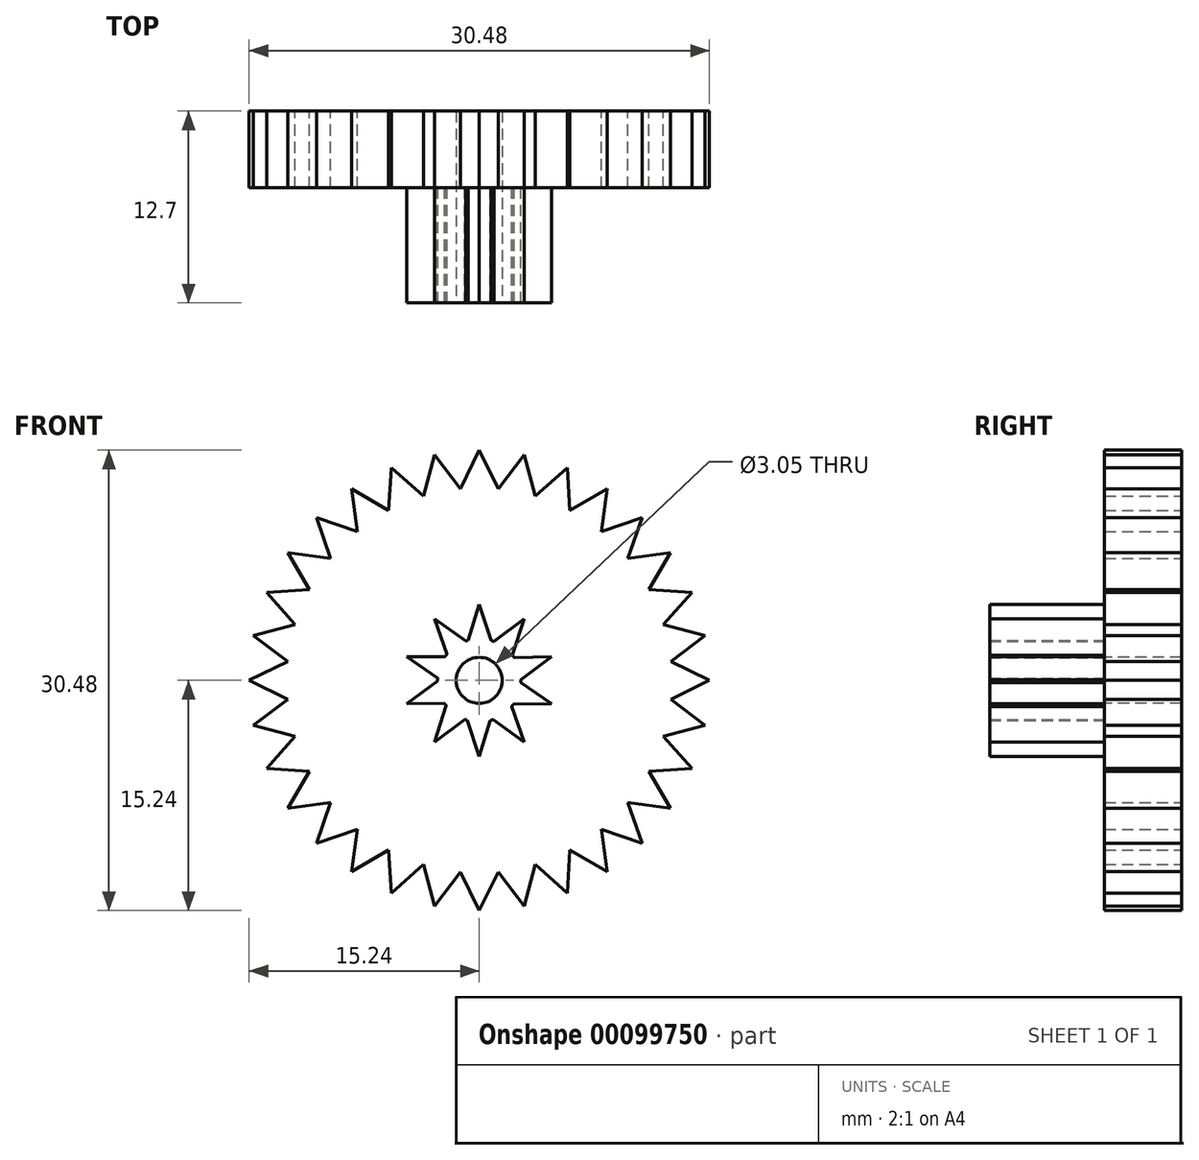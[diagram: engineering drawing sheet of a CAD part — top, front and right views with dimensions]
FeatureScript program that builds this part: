
annotation { "Feature Type Name" : "Feature", "Feature Type Description" : "" }
export const myFeature = defineFeature(function(context is Context, id is Id, definition is map)
    precondition{}
    {
        {
            var Q0;
            Q0=qCreatedBy(makeId("Front.planeOp"),FACE);
            var sketch = newSketch(context, id + "F0", { "sketchPlane" : qUnion([Q0])});
            skCircle(sketch, "E0", {"center": v(0, 0) * mm, "radius": 12.7 * mm});
            skLineSegment(sketch, "E1", {"start": v(1.27, 12.64) * mm, "end": v(0, 15.24) * mm});
            skLineSegment(sketch, "E2", {"start": v(0, 15.24) * mm, "end": v(-1.27, 12.64) * mm});
            skLineSegment(sketch, "E3.1.0", {"start": v(-2.97, 14.95) * mm, "end": v(-3.71, 12.15) * mm});
            skLineSegment(sketch, "E3.1.1", {"start": v(-1.22, 12.64) * mm, "end": v(-2.97, 14.95) * mm});
            skLineSegment(sketch, "E3.2.0", {"start": v(-5.83, 14.08) * mm, "end": v(-6, 11.19) * mm});
            skLineSegment(sketch, "E3.2.1", {"start": v(-3.66, 12.16) * mm, "end": v(-5.83, 14.08) * mm});
            skLineSegment(sketch, "E4.2.3.0", {"start": v(-8.47, 12.67) * mm, "end": v(-8.08, 9.8) * mm});
            skLineSegment(sketch, "E4.3.3.0", {"start": v(-5.96, 11.21) * mm, "end": v(-8.47, 12.67) * mm});
            skLineSegment(sketch, "E4.2.4.0", {"start": v(-10.78, 10.78) * mm, "end": v(-9.83, 8.04) * mm});
            skLineSegment(sketch, "E4.3.4.0", {"start": v(-8.04, 9.83) * mm, "end": v(-10.78, 10.78) * mm});
            skLineSegment(sketch, "E4.2.5.0", {"start": v(-12.67, 8.47) * mm, "end": v(-11.21, 5.96) * mm});
            skLineSegment(sketch, "E4.3.5.0", {"start": v(-9.8, 8.08) * mm, "end": v(-12.67, 8.47) * mm});
            skLineSegment(sketch, "E4.2.6.0", {"start": v(-14.08, 5.83) * mm, "end": v(-12.16, 3.66) * mm});
            skLineSegment(sketch, "E4.3.6.0", {"start": v(-11.19, 6) * mm, "end": v(-14.08, 5.83) * mm});
            skLineSegment(sketch, "E4.2.7.0", {"start": v(-14.95, 2.97) * mm, "end": v(-12.64, 1.22) * mm});
            skLineSegment(sketch, "E4.3.7.0", {"start": v(-12.15, 3.71) * mm, "end": v(-14.95, 2.97) * mm});
            skLineSegment(sketch, "E4.2.8.0", {"start": v(-15.24, 0) * mm, "end": v(-12.64, -1.27) * mm});
            skLineSegment(sketch, "E4.3.8.0", {"start": v(-12.64, 1.27) * mm, "end": v(-15.24, 0) * mm});
            skLineSegment(sketch, "E4.2.9.0", {"start": v(-14.95, -2.97) * mm, "end": v(-12.15, -3.71) * mm});
            skLineSegment(sketch, "E4.3.9.0", {"start": v(-12.64, -1.22) * mm, "end": v(-14.95, -2.97) * mm});
            skLineSegment(sketch, "E4.2.10.0", {"start": v(-14.08, -5.83) * mm, "end": v(-11.19, -6) * mm});
            skLineSegment(sketch, "E4.3.10.0", {"start": v(-12.16, -3.66) * mm, "end": v(-14.08, -5.83) * mm});
            skLineSegment(sketch, "E4.2.11.0", {"start": v(-12.67, -8.47) * mm, "end": v(-9.8, -8.08) * mm});
            skLineSegment(sketch, "E4.3.11.0", {"start": v(-11.21, -5.96) * mm, "end": v(-12.67, -8.47) * mm});
            skLineSegment(sketch, "E4.2.12.0", {"start": v(-10.78, -10.78) * mm, "end": v(-8.04, -9.83) * mm});
            skLineSegment(sketch, "E4.3.12.0", {"start": v(-9.83, -8.04) * mm, "end": v(-10.78, -10.78) * mm});
            skLineSegment(sketch, "E4.2.13.0", {"start": v(-8.47, -12.67) * mm, "end": v(-5.96, -11.21) * mm});
            skLineSegment(sketch, "E4.3.13.0", {"start": v(-8.08, -9.8) * mm, "end": v(-8.47, -12.67) * mm});
            skLineSegment(sketch, "E4.2.14.0", {"start": v(-5.83, -14.08) * mm, "end": v(-3.66, -12.16) * mm});
            skLineSegment(sketch, "E4.3.14.0", {"start": v(-6, -11.19) * mm, "end": v(-5.83, -14.08) * mm});
            skLineSegment(sketch, "E4.2.15.0", {"start": v(-2.97, -14.95) * mm, "end": v(-1.22, -12.64) * mm});
            skLineSegment(sketch, "E4.3.15.0", {"start": v(-3.71, -12.15) * mm, "end": v(-2.97, -14.95) * mm});
            skLineSegment(sketch, "E4.2.16.0", {"start": v(0, -15.24) * mm, "end": v(1.27, -12.64) * mm});
            skLineSegment(sketch, "E4.3.16.0", {"start": v(-1.27, -12.64) * mm, "end": v(0, -15.24) * mm});
            skLineSegment(sketch, "E4.2.17.0", {"start": v(2.97, -14.95) * mm, "end": v(3.71, -12.15) * mm});
            skLineSegment(sketch, "E4.3.17.0", {"start": v(1.22, -12.64) * mm, "end": v(2.97, -14.95) * mm});
            skLineSegment(sketch, "E4.2.18.0", {"start": v(5.83, -14.08) * mm, "end": v(6, -11.19) * mm});
            skLineSegment(sketch, "E4.3.18.0", {"start": v(3.66, -12.16) * mm, "end": v(5.83, -14.08) * mm});
            skLineSegment(sketch, "E4.2.19.0", {"start": v(8.47, -12.67) * mm, "end": v(8.08, -9.8) * mm});
            skLineSegment(sketch, "E4.3.19.0", {"start": v(5.96, -11.21) * mm, "end": v(8.47, -12.67) * mm});
            skLineSegment(sketch, "E4.2.20.0", {"start": v(10.78, -10.78) * mm, "end": v(9.83, -8.04) * mm});
            skLineSegment(sketch, "E4.3.20.0", {"start": v(8.04, -9.83) * mm, "end": v(10.78, -10.78) * mm});
            skLineSegment(sketch, "E4.2.21.0", {"start": v(12.67, -8.47) * mm, "end": v(11.21, -5.96) * mm});
            skLineSegment(sketch, "E4.3.21.0", {"start": v(9.8, -8.08) * mm, "end": v(12.67, -8.47) * mm});
            skLineSegment(sketch, "E4.2.22.0", {"start": v(14.08, -5.83) * mm, "end": v(12.16, -3.66) * mm});
            skLineSegment(sketch, "E4.3.22.0", {"start": v(11.19, -6) * mm, "end": v(14.08, -5.83) * mm});
            skLineSegment(sketch, "E4.2.23.0", {"start": v(14.95, -2.97) * mm, "end": v(12.64, -1.22) * mm});
            skLineSegment(sketch, "E4.3.23.0", {"start": v(12.15, -3.71) * mm, "end": v(14.95, -2.97) * mm});
            skLineSegment(sketch, "E4.2.24.0", {"start": v(15.24, 0) * mm, "end": v(12.64, 1.27) * mm});
            skLineSegment(sketch, "E4.3.24.0", {"start": v(12.64, -1.27) * mm, "end": v(15.24, 0) * mm});
            skLineSegment(sketch, "E4.2.25.0", {"start": v(14.95, 2.97) * mm, "end": v(12.15, 3.71) * mm});
            skLineSegment(sketch, "E4.3.25.0", {"start": v(12.64, 1.22) * mm, "end": v(14.95, 2.97) * mm});
            skLineSegment(sketch, "E4.2.26.0", {"start": v(14.08, 5.83) * mm, "end": v(11.19, 6) * mm});
            skLineSegment(sketch, "E4.3.26.0", {"start": v(12.16, 3.66) * mm, "end": v(14.08, 5.83) * mm});
            skLineSegment(sketch, "E4.2.27.0", {"start": v(12.67, 8.47) * mm, "end": v(9.8, 8.08) * mm});
            skLineSegment(sketch, "E4.3.27.0", {"start": v(11.21, 5.96) * mm, "end": v(12.67, 8.47) * mm});
            skLineSegment(sketch, "E4.2.28.0", {"start": v(10.78, 10.78) * mm, "end": v(8.04, 9.83) * mm});
            skLineSegment(sketch, "E4.3.28.0", {"start": v(9.83, 8.04) * mm, "end": v(10.78, 10.78) * mm});
            skLineSegment(sketch, "E4.2.29.0", {"start": v(8.47, 12.67) * mm, "end": v(5.96, 11.21) * mm});
            skLineSegment(sketch, "E4.3.29.0", {"start": v(8.08, 9.8) * mm, "end": v(8.47, 12.67) * mm});
            skLineSegment(sketch, "E4.2.30.0", {"start": v(5.83, 14.08) * mm, "end": v(3.66, 12.16) * mm});
            skLineSegment(sketch, "E4.3.30.0", {"start": v(6, 11.19) * mm, "end": v(5.83, 14.08) * mm});
            skLineSegment(sketch, "E4.2.31.0", {"start": v(2.97, 14.95) * mm, "end": v(1.22, 12.64) * mm});
            skLineSegment(sketch, "E4.3.31.0", {"start": v(3.71, 12.15) * mm, "end": v(2.97, 14.95) * mm});
            skSolve(sketch);
        }
        {
            var Q0;
            {var subQ3=sQuery(id+"F0.wireOp",EDGE,"E3.1.0");var subQ5=sQuery(id+"F0.wireOp",EDGE,"E0");var subQ6=makeQuery(id+"F0.imprint","INTERSECT",VERTEX,{"derivedFrom":[subQ5,subQ3]});Q0=makeQuery(id+"F0.imprint","IMPRINT",FACE,{"disambiguationData":[TD([[makeQuery(id+"F0.imprint","IMPRINT",EDGE,{"disambiguationData":[TD([[subQ6,-1.0]])],"derivedFrom":subQ5}),-1.0]])]});}
            var Q1;
            {var subQ3=sQuery(id+"F0.wireOp",EDGE,"E4.2.17.0");var subQ7=sQuery(id+"F0.wireOp",EDGE,"E0");var subQ8=makeQuery(id+"F0.imprint","INTERSECT",VERTEX,{"derivedFrom":[subQ7,subQ3]});Q1=makeQuery(id+"F0.imprint","IMPRINT",FACE,{"disambiguationData":[TD([[makeQuery(id+"F0.imprint","IMPRINT",EDGE,{"disambiguationData":[TD([[subQ8,-1.0]])],"derivedFrom":subQ7}),-1.0]])]});}
            var Q2;
            {var subQ3=sQuery(id+"F0.wireOp",EDGE,"E4.2.9.0");var subQ7=sQuery(id+"F0.wireOp",EDGE,"E0");var subQ8=makeQuery(id+"F0.imprint","INTERSECT",VERTEX,{"derivedFrom":[subQ7,subQ3]});Q2=makeQuery(id+"F0.imprint","IMPRINT",FACE,{"disambiguationData":[TD([[makeQuery(id+"F0.imprint","IMPRINT",EDGE,{"disambiguationData":[TD([[subQ8,-1.0]])],"derivedFrom":subQ7}),-1.0]])]});}
            var Q3;
            {var subQ5=sQuery(id+"F0.wireOp",EDGE,"E4.2.22.0");var subQ7=sQuery(id+"F0.wireOp",EDGE,"E0");var subQ8=makeQuery(id+"F0.imprint","INTERSECT",VERTEX,{"derivedFrom":[subQ7,subQ5]});Q3=makeQuery(id+"F0.imprint","IMPRINT",FACE,{"disambiguationData":[TD([[makeQuery(id+"F0.imprint","IMPRINT",EDGE,{"disambiguationData":[TD([[subQ8,-1.0]])],"derivedFrom":subQ7}),-1.0]])]});}
            var Q4;
            {var subQ3=sQuery(id+"F0.wireOp",EDGE,"E4.2.14.0");var subQ7=sQuery(id+"F0.wireOp",EDGE,"E0");var subQ8=makeQuery(id+"F0.imprint","INTERSECT",VERTEX,{"derivedFrom":[subQ7,subQ3]});Q4=makeQuery(id+"F0.imprint","IMPRINT",FACE,{"disambiguationData":[TD([[makeQuery(id+"F0.imprint","IMPRINT",EDGE,{"disambiguationData":[TD([[subQ8,-1.0]])],"derivedFrom":subQ7}),-1.0]])]});}
            var Q5;
            {var subQ3=sQuery(id+"F0.wireOp",EDGE,"E4.2.6.0");var subQ7=sQuery(id+"F0.wireOp",EDGE,"E0");var subQ8=makeQuery(id+"F0.imprint","INTERSECT",VERTEX,{"derivedFrom":[subQ7,subQ3]});Q5=makeQuery(id+"F0.imprint","IMPRINT",FACE,{"disambiguationData":[TD([[makeQuery(id+"F0.imprint","IMPRINT",EDGE,{"disambiguationData":[TD([[subQ8,-1.0]])],"derivedFrom":subQ7}),-1.0]])]});}
            var Q6;
            {var subQ0=sQuery(id+"F0.wireOp",EDGE,"E3.1.1");var subQ1=sQuery(id+"F0.wireOp",EDGE,"E0");var subQ2=makeQuery(id+"F0.imprint","INTERSECT",VERTEX,{"derivedFrom":[subQ1,subQ0]});Q6=makeQuery(id+"F0.imprint","IMPRINT",FACE,{"disambiguationData":[TD([[makeQuery(id+"F0.imprint","IMPRINT",EDGE,{"disambiguationData":[TD([[subQ2,1.0]])],"derivedFrom":subQ1}),-1.0]])]});}
            var Q7;
            {var subQ3=sQuery(id+"F0.wireOp",EDGE,"E1");var subQ6=sQuery(id+"F0.wireOp",EDGE,"E0");var subQ9=makeQuery(id+"F0.imprint","INTERSECT",VERTEX,{"derivedFrom":[subQ6,subQ3]});Q7=makeQuery(id+"F0.imprint","IMPRINT",FACE,{"disambiguationData":[TD([[makeQuery(id+"F0.imprint","IMPRINT",EDGE,{"disambiguationData":[TD([[subQ9,1.0]])],"derivedFrom":subQ6}),-1.0]])]});}
            var Q8;
            {var subQ0=sQuery(id+"F0.wireOp",EDGE,"E0");var subQ35=makeQuery(id+"F0.imprint","INTERSECT",VERTEX,{"derivedFrom":[subQ0,sQuery(id+"F0.wireOp",EDGE,"E4.2.24.0")]});Q8=makeQuery(id+"F0.imprint","IMPRINT",FACE,{"disambiguationData":[TD([[makeQuery(id+"F0.imprint","IMPRINT",EDGE,{"disambiguationData":[TD([[subQ35,1.0]])],"derivedFrom":subQ0}),1.0]])]});}
            var Q9;
            {var subQ3=sQuery(id+"F0.wireOp",EDGE,"E4.2.24.0");var subQ7=sQuery(id+"F0.wireOp",EDGE,"E0");var subQ8=makeQuery(id+"F0.imprint","INTERSECT",VERTEX,{"derivedFrom":[subQ7,subQ3]});Q9=makeQuery(id+"F0.imprint","IMPRINT",FACE,{"disambiguationData":[TD([[makeQuery(id+"F0.imprint","IMPRINT",EDGE,{"disambiguationData":[TD([[subQ8,-1.0]])],"derivedFrom":subQ7}),-1.0]])]});}
            var Q10;
            {var subQ3=sQuery(id+"F0.wireOp",EDGE,"E4.2.25.0");var subQ5=sQuery(id+"F0.wireOp",EDGE,"E0");var subQ6=makeQuery(id+"F0.imprint","INTERSECT",VERTEX,{"derivedFrom":[subQ5,subQ3]});Q10=makeQuery(id+"F0.imprint","IMPRINT",FACE,{"disambiguationData":[TD([[makeQuery(id+"F0.imprint","IMPRINT",EDGE,{"disambiguationData":[TD([[subQ6,-1.0]])],"derivedFrom":subQ5}),-1.0]])]});}
            var Q11;
            {var subQ5=sQuery(id+"F0.wireOp",EDGE,"E4.2.26.0");var subQ7=sQuery(id+"F0.wireOp",EDGE,"E0");var subQ8=makeQuery(id+"F0.imprint","INTERSECT",VERTEX,{"derivedFrom":[subQ7,subQ5]});Q11=makeQuery(id+"F0.imprint","IMPRINT",FACE,{"disambiguationData":[TD([[makeQuery(id+"F0.imprint","IMPRINT",EDGE,{"disambiguationData":[TD([[subQ8,-1.0]])],"derivedFrom":subQ7}),-1.0]])]});}
            var Q12;
            {var subQ5=sQuery(id+"F0.wireOp",EDGE,"E4.2.27.0");var subQ6=sQuery(id+"F0.wireOp",EDGE,"E0");var subQ7=makeQuery(id+"F0.imprint","INTERSECT",VERTEX,{"derivedFrom":[subQ6,subQ5]});Q12=makeQuery(id+"F0.imprint","IMPRINT",FACE,{"disambiguationData":[TD([[makeQuery(id+"F0.imprint","IMPRINT",EDGE,{"disambiguationData":[TD([[subQ7,-1.0]])],"derivedFrom":subQ6}),-1.0]])]});}
            var Q13;
            {var subQ3=sQuery(id+"F0.wireOp",EDGE,"E4.2.28.0");var subQ7=sQuery(id+"F0.wireOp",EDGE,"E0");var subQ8=makeQuery(id+"F0.imprint","INTERSECT",VERTEX,{"derivedFrom":[subQ7,subQ3]});Q13=makeQuery(id+"F0.imprint","IMPRINT",FACE,{"disambiguationData":[TD([[makeQuery(id+"F0.imprint","IMPRINT",EDGE,{"disambiguationData":[TD([[subQ8,-1.0]])],"derivedFrom":subQ7}),-1.0]])]});}
            var Q14;
            {var subQ5=sQuery(id+"F0.wireOp",EDGE,"E4.2.29.0");var subQ6=sQuery(id+"F0.wireOp",EDGE,"E0");var subQ7=makeQuery(id+"F0.imprint","INTERSECT",VERTEX,{"derivedFrom":[subQ6,subQ5]});Q14=makeQuery(id+"F0.imprint","IMPRINT",FACE,{"disambiguationData":[TD([[makeQuery(id+"F0.imprint","IMPRINT",EDGE,{"disambiguationData":[TD([[subQ7,-1.0]])],"derivedFrom":subQ6}),-1.0]])]});}
            var Q15;
            {var subQ3=sQuery(id+"F0.wireOp",EDGE,"E4.2.21.0");var subQ7=sQuery(id+"F0.wireOp",EDGE,"E0");var subQ8=makeQuery(id+"F0.imprint","INTERSECT",VERTEX,{"derivedFrom":[subQ7,subQ3]});Q15=makeQuery(id+"F0.imprint","IMPRINT",FACE,{"disambiguationData":[TD([[makeQuery(id+"F0.imprint","IMPRINT",EDGE,{"disambiguationData":[TD([[subQ8,-1.0]])],"derivedFrom":subQ7}),-1.0]])]});}
            var Q16;
            {var subQ3=sQuery(id+"F0.wireOp",EDGE,"E4.2.13.0");var subQ5=sQuery(id+"F0.wireOp",EDGE,"E0");var subQ6=makeQuery(id+"F0.imprint","INTERSECT",VERTEX,{"derivedFrom":[subQ5,subQ3]});Q16=makeQuery(id+"F0.imprint","IMPRINT",FACE,{"disambiguationData":[TD([[makeQuery(id+"F0.imprint","IMPRINT",EDGE,{"disambiguationData":[TD([[subQ6,-1.0]])],"derivedFrom":subQ5}),-1.0]])]});}
            var Q17;
            {var subQ3=sQuery(id+"F0.wireOp",EDGE,"E4.2.5.0");var subQ5=sQuery(id+"F0.wireOp",EDGE,"E0");var subQ6=makeQuery(id+"F0.imprint","INTERSECT",VERTEX,{"derivedFrom":[subQ5,subQ3]});Q17=makeQuery(id+"F0.imprint","IMPRINT",FACE,{"disambiguationData":[TD([[makeQuery(id+"F0.imprint","IMPRINT",EDGE,{"disambiguationData":[TD([[subQ6,-1.0]])],"derivedFrom":subQ5}),-1.0]])]});}
            var Q18;
            {var subQ3=sQuery(id+"F0.wireOp",EDGE,"E4.2.19.0");var subQ5=sQuery(id+"F0.wireOp",EDGE,"E0");var subQ6=makeQuery(id+"F0.imprint","INTERSECT",VERTEX,{"derivedFrom":[subQ5,subQ3]});Q18=makeQuery(id+"F0.imprint","IMPRINT",FACE,{"disambiguationData":[TD([[makeQuery(id+"F0.imprint","IMPRINT",EDGE,{"disambiguationData":[TD([[subQ6,-1.0]])],"derivedFrom":subQ5}),-1.0]])]});}
            var Q19;
            {var subQ5=sQuery(id+"F0.wireOp",EDGE,"E4.2.11.0");var subQ6=sQuery(id+"F0.wireOp",EDGE,"E0");var subQ7=makeQuery(id+"F0.imprint","INTERSECT",VERTEX,{"derivedFrom":[subQ6,subQ5]});Q19=makeQuery(id+"F0.imprint","IMPRINT",FACE,{"disambiguationData":[TD([[makeQuery(id+"F0.imprint","IMPRINT",EDGE,{"disambiguationData":[TD([[subQ7,-1.0]])],"derivedFrom":subQ6}),-1.0]])]});}
            var Q20;
            {var subQ5=sQuery(id+"F0.wireOp",EDGE,"E4.2.3.0");var subQ6=sQuery(id+"F0.wireOp",EDGE,"E0");var subQ7=makeQuery(id+"F0.imprint","INTERSECT",VERTEX,{"derivedFrom":[subQ6,subQ5]});Q20=makeQuery(id+"F0.imprint","IMPRINT",FACE,{"disambiguationData":[TD([[makeQuery(id+"F0.imprint","IMPRINT",EDGE,{"disambiguationData":[TD([[subQ7,-1.0]])],"derivedFrom":subQ6}),-1.0]])]});}
            var Q21;
            {var subQ3=sQuery(id+"F0.wireOp",EDGE,"E3.2.0");var subQ7=sQuery(id+"F0.wireOp",EDGE,"E0");var subQ9=makeQuery(id+"F0.imprint","INTERSECT",VERTEX,{"derivedFrom":[subQ7,subQ3]});Q21=makeQuery(id+"F0.imprint","IMPRINT",FACE,{"disambiguationData":[TD([[makeQuery(id+"F0.imprint","IMPRINT",EDGE,{"disambiguationData":[TD([[subQ9,-1.0]])],"derivedFrom":subQ7}),-1.0]])]});}
            var Q22;
            {var subQ3=sQuery(id+"F0.wireOp",EDGE,"E4.2.18.0");var subQ7=sQuery(id+"F0.wireOp",EDGE,"E0");var subQ8=makeQuery(id+"F0.imprint","INTERSECT",VERTEX,{"derivedFrom":[subQ7,subQ3]});Q22=makeQuery(id+"F0.imprint","IMPRINT",FACE,{"disambiguationData":[TD([[makeQuery(id+"F0.imprint","IMPRINT",EDGE,{"disambiguationData":[TD([[subQ8,-1.0]])],"derivedFrom":subQ7}),-1.0]])]});}
            var Q23;
            {var subQ3=sQuery(id+"F0.wireOp",EDGE,"E4.2.10.0");var subQ7=sQuery(id+"F0.wireOp",EDGE,"E0");var subQ8=makeQuery(id+"F0.imprint","INTERSECT",VERTEX,{"derivedFrom":[subQ7,subQ3]});Q23=makeQuery(id+"F0.imprint","IMPRINT",FACE,{"disambiguationData":[TD([[makeQuery(id+"F0.imprint","IMPRINT",EDGE,{"disambiguationData":[TD([[subQ8,-1.0]])],"derivedFrom":subQ7}),-1.0]])]});}
            var Q24;
            {var subQ0=sQuery(id+"F0.wireOp",EDGE,"E2");var subQ1=sQuery(id+"F0.wireOp",EDGE,"E0");var subQ2=makeQuery(id+"F0.imprint","INTERSECT",VERTEX,{"derivedFrom":[subQ1,subQ0]});Q24=makeQuery(id+"F0.imprint","IMPRINT",FACE,{"disambiguationData":[TD([[makeQuery(id+"F0.imprint","IMPRINT",EDGE,{"disambiguationData":[TD([[subQ2,-1.0]])],"derivedFrom":subQ1}),-1.0]])]});}
            var Q25;
            {var subQ0=sQuery(id+"F0.wireOp",EDGE,"E4.2.16.0");var subQ1=sQuery(id+"F0.wireOp",EDGE,"E0");var subQ2=makeQuery(id+"F0.imprint","INTERSECT",VERTEX,{"derivedFrom":[subQ1,subQ0]});Q25=makeQuery(id+"F0.imprint","IMPRINT",FACE,{"disambiguationData":[TD([[makeQuery(id+"F0.imprint","IMPRINT",EDGE,{"disambiguationData":[TD([[subQ2,-1.0]])],"derivedFrom":subQ1}),-1.0]])]});}
            var Q26;
            {var subQ3=sQuery(id+"F0.wireOp",EDGE,"E4.2.8.0");var subQ5=sQuery(id+"F0.wireOp",EDGE,"E0");var subQ6=makeQuery(id+"F0.imprint","INTERSECT",VERTEX,{"derivedFrom":[subQ5,subQ3]});Q26=makeQuery(id+"F0.imprint","IMPRINT",FACE,{"disambiguationData":[TD([[makeQuery(id+"F0.imprint","IMPRINT",EDGE,{"disambiguationData":[TD([[subQ6,-1.0]])],"derivedFrom":subQ5}),-1.0]])]});}
            var Q27;
            {var subQ3=sQuery(id+"F0.wireOp",EDGE,"E4.2.7.0");var subQ7=sQuery(id+"F0.wireOp",EDGE,"E0");var subQ8=makeQuery(id+"F0.imprint","INTERSECT",VERTEX,{"derivedFrom":[subQ7,subQ3]});Q27=makeQuery(id+"F0.imprint","IMPRINT",FACE,{"disambiguationData":[TD([[makeQuery(id+"F0.imprint","IMPRINT",EDGE,{"disambiguationData":[TD([[subQ8,-1.0]])],"derivedFrom":subQ7}),-1.0]])]});}
            var Q28;
            {var subQ5=sQuery(id+"F0.wireOp",EDGE,"E4.2.20.0");var subQ6=sQuery(id+"F0.wireOp",EDGE,"E0");var subQ7=makeQuery(id+"F0.imprint","INTERSECT",VERTEX,{"derivedFrom":[subQ6,subQ5]});Q28=makeQuery(id+"F0.imprint","IMPRINT",FACE,{"disambiguationData":[TD([[makeQuery(id+"F0.imprint","IMPRINT",EDGE,{"disambiguationData":[TD([[subQ7,-1.0]])],"derivedFrom":subQ6}),-1.0]])]});}
            var Q29;
            {var subQ3=sQuery(id+"F0.wireOp",EDGE,"E4.2.12.0");var subQ7=sQuery(id+"F0.wireOp",EDGE,"E0");var subQ8=makeQuery(id+"F0.imprint","INTERSECT",VERTEX,{"derivedFrom":[subQ7,subQ3]});Q29=makeQuery(id+"F0.imprint","IMPRINT",FACE,{"disambiguationData":[TD([[makeQuery(id+"F0.imprint","IMPRINT",EDGE,{"disambiguationData":[TD([[subQ8,-1.0]])],"derivedFrom":subQ7}),-1.0]])]});}
            var Q30;
            {var subQ5=sQuery(id+"F0.wireOp",EDGE,"E0");var subQ7=sQuery(id+"F0.wireOp",EDGE,"E4.2.4.0");var subQ9=makeQuery(id+"F0.imprint","INTERSECT",VERTEX,{"derivedFrom":[subQ5,subQ7]});Q30=makeQuery(id+"F0.imprint","IMPRINT",FACE,{"disambiguationData":[TD([[makeQuery(id+"F0.imprint","IMPRINT",EDGE,{"disambiguationData":[TD([[subQ9,-1.0]])],"derivedFrom":subQ5}),-1.0]])]});}
            var Q31;
            {var subQ3=sQuery(id+"F0.wireOp",EDGE,"E4.2.15.0");var subQ7=sQuery(id+"F0.wireOp",EDGE,"E0");var subQ8=makeQuery(id+"F0.imprint","INTERSECT",VERTEX,{"derivedFrom":[subQ7,subQ3]});Q31=makeQuery(id+"F0.imprint","IMPRINT",FACE,{"disambiguationData":[TD([[makeQuery(id+"F0.imprint","IMPRINT",EDGE,{"disambiguationData":[TD([[subQ8,-1.0]])],"derivedFrom":subQ7}),-1.0]])]});}
            var Q32;
            {var subQ0=sQuery(id+"F0.wireOp",EDGE,"E4.2.19.0");var subQ1=sQuery(id+"F0.wireOp",EDGE,"E0");var subQ2=makeQuery(id+"F0.imprint","INTERSECT",VERTEX,{"derivedFrom":[subQ1,subQ0]});Q32=makeQuery(id+"F0.imprint","IMPRINT",FACE,{"disambiguationData":[TD([[makeQuery(id+"F0.imprint","IMPRINT",EDGE,{"disambiguationData":[TD([[subQ2,1.0]])],"derivedFrom":subQ1}),-1.0]])]});}
            var Q33;
            {var subQ0=sQuery(id+"F0.wireOp",EDGE,"E4.2.28.0");var subQ1=sQuery(id+"F0.wireOp",EDGE,"E0");var subQ2=makeQuery(id+"F0.imprint","INTERSECT",VERTEX,{"derivedFrom":[subQ1,subQ0]});Q33=makeQuery(id+"F0.imprint","IMPRINT",FACE,{"disambiguationData":[TD([[makeQuery(id+"F0.imprint","IMPRINT",EDGE,{"disambiguationData":[TD([[subQ2,1.0]])],"derivedFrom":subQ1}),-1.0]])]});}
            var Q34;
            {var subQ3=sQuery(id+"F0.wireOp",EDGE,"E4.2.23.0");var subQ7=sQuery(id+"F0.wireOp",EDGE,"E0");var subQ8=makeQuery(id+"F0.imprint","INTERSECT",VERTEX,{"derivedFrom":[subQ7,subQ3]});Q34=makeQuery(id+"F0.imprint","IMPRINT",FACE,{"disambiguationData":[TD([[makeQuery(id+"F0.imprint","IMPRINT",EDGE,{"disambiguationData":[TD([[subQ8,-1.0]])],"derivedFrom":subQ7}),-1.0]])]});}
            var Q35;
            {var subQ0=sQuery(id+"F0.wireOp",EDGE,"E4.2.21.0");var subQ1=sQuery(id+"F0.wireOp",EDGE,"E0");var subQ2=makeQuery(id+"F0.imprint","INTERSECT",VERTEX,{"derivedFrom":[subQ1,subQ0]});Q35=makeQuery(id+"F0.imprint","IMPRINT",FACE,{"disambiguationData":[TD([[makeQuery(id+"F0.imprint","IMPRINT",EDGE,{"disambiguationData":[TD([[subQ2,1.0]])],"derivedFrom":subQ1}),-1.0]])]});}
            var Q36;
            {var subQ0=sQuery(id+"F0.wireOp",EDGE,"E4.2.13.0");var subQ1=sQuery(id+"F0.wireOp",EDGE,"E0");var subQ2=makeQuery(id+"F0.imprint","INTERSECT",VERTEX,{"derivedFrom":[subQ1,subQ0]});Q36=makeQuery(id+"F0.imprint","IMPRINT",FACE,{"disambiguationData":[TD([[makeQuery(id+"F0.imprint","IMPRINT",EDGE,{"disambiguationData":[TD([[subQ2,1.0]])],"derivedFrom":subQ1}),-1.0]])]});}
            var Q37;
            {var subQ0=sQuery(id+"F0.wireOp",EDGE,"E4.2.5.0");var subQ1=sQuery(id+"F0.wireOp",EDGE,"E0");var subQ2=makeQuery(id+"F0.imprint","INTERSECT",VERTEX,{"derivedFrom":[subQ1,subQ0]});Q37=makeQuery(id+"F0.imprint","IMPRINT",FACE,{"disambiguationData":[TD([[makeQuery(id+"F0.imprint","IMPRINT",EDGE,{"disambiguationData":[TD([[subQ2,1.0]])],"derivedFrom":subQ1}),-1.0]])]});}
            var Q38;
            {var subQ0=sQuery(id+"F0.wireOp",EDGE,"E4.2.11.0");var subQ1=sQuery(id+"F0.wireOp",EDGE,"E0");var subQ2=makeQuery(id+"F0.imprint","INTERSECT",VERTEX,{"derivedFrom":[subQ1,subQ0]});Q38=makeQuery(id+"F0.imprint","IMPRINT",FACE,{"disambiguationData":[TD([[makeQuery(id+"F0.imprint","IMPRINT",EDGE,{"disambiguationData":[TD([[subQ2,1.0]])],"derivedFrom":subQ1}),-1.0]])]});}
            var Q39;
            {var subQ0=sQuery(id+"F0.wireOp",EDGE,"E4.2.3.0");var subQ1=sQuery(id+"F0.wireOp",EDGE,"E0");var subQ2=makeQuery(id+"F0.imprint","INTERSECT",VERTEX,{"derivedFrom":[subQ1,subQ0]});Q39=makeQuery(id+"F0.imprint","IMPRINT",FACE,{"disambiguationData":[TD([[makeQuery(id+"F0.imprint","IMPRINT",EDGE,{"disambiguationData":[TD([[subQ2,1.0]])],"derivedFrom":subQ1}),-1.0]])]});}
            var Q40;
            {var subQ0=sQuery(id+"F0.wireOp",EDGE,"E3.2.0");var subQ1=sQuery(id+"F0.wireOp",EDGE,"E0");var subQ2=makeQuery(id+"F0.imprint","INTERSECT",VERTEX,{"derivedFrom":[subQ1,subQ0]});Q40=makeQuery(id+"F0.imprint","IMPRINT",FACE,{"disambiguationData":[TD([[makeQuery(id+"F0.imprint","IMPRINT",EDGE,{"disambiguationData":[TD([[subQ2,1.0]])],"derivedFrom":subQ1}),-1.0]])]});}
            var Q41;
            {var subQ0=sQuery(id+"F0.wireOp",EDGE,"E4.2.18.0");var subQ1=sQuery(id+"F0.wireOp",EDGE,"E0");var subQ2=makeQuery(id+"F0.imprint","INTERSECT",VERTEX,{"derivedFrom":[subQ1,subQ0]});Q41=makeQuery(id+"F0.imprint","IMPRINT",FACE,{"disambiguationData":[TD([[makeQuery(id+"F0.imprint","IMPRINT",EDGE,{"disambiguationData":[TD([[subQ2,1.0]])],"derivedFrom":subQ1}),-1.0]])]});}
            var Q42;
            {var subQ0=sQuery(id+"F0.wireOp",EDGE,"E4.2.10.0");var subQ1=sQuery(id+"F0.wireOp",EDGE,"E0");var subQ2=makeQuery(id+"F0.imprint","INTERSECT",VERTEX,{"derivedFrom":[subQ1,subQ0]});Q42=makeQuery(id+"F0.imprint","IMPRINT",FACE,{"disambiguationData":[TD([[makeQuery(id+"F0.imprint","IMPRINT",EDGE,{"disambiguationData":[TD([[subQ2,1.0]])],"derivedFrom":subQ1}),-1.0]])]});}
            var Q43;
            {var subQ0=sQuery(id+"F0.wireOp",EDGE,"E2");var subQ1=sQuery(id+"F0.wireOp",EDGE,"E0");var subQ2=makeQuery(id+"F0.imprint","INTERSECT",VERTEX,{"derivedFrom":[subQ1,subQ0]});Q43=makeQuery(id+"F0.imprint","IMPRINT",FACE,{"disambiguationData":[TD([[makeQuery(id+"F0.imprint","IMPRINT",EDGE,{"disambiguationData":[TD([[subQ2,1.0]])],"derivedFrom":subQ1}),-1.0]])]});}
            var Q44;
            {var subQ0=sQuery(id+"F0.wireOp",EDGE,"E4.2.24.0");var subQ1=sQuery(id+"F0.wireOp",EDGE,"E0");var subQ2=makeQuery(id+"F0.imprint","INTERSECT",VERTEX,{"derivedFrom":[subQ1,subQ0]});Q44=makeQuery(id+"F0.imprint","IMPRINT",FACE,{"disambiguationData":[TD([[makeQuery(id+"F0.imprint","IMPRINT",EDGE,{"disambiguationData":[TD([[subQ2,1.0]])],"derivedFrom":subQ1}),-1.0]])]});}
            var Q45;
            {var subQ0=sQuery(id+"F0.wireOp",EDGE,"E4.2.23.0");var subQ1=sQuery(id+"F0.wireOp",EDGE,"E0");var subQ2=makeQuery(id+"F0.imprint","INTERSECT",VERTEX,{"derivedFrom":[subQ1,subQ0]});Q45=makeQuery(id+"F0.imprint","IMPRINT",FACE,{"disambiguationData":[TD([[makeQuery(id+"F0.imprint","IMPRINT",EDGE,{"disambiguationData":[TD([[subQ2,1.0]])],"derivedFrom":subQ1}),-1.0]])]});}
            var Q46;
            {var subQ0=sQuery(id+"F0.wireOp",EDGE,"E4.2.7.0");var subQ1=sQuery(id+"F0.wireOp",EDGE,"E0");var subQ2=makeQuery(id+"F0.imprint","INTERSECT",VERTEX,{"derivedFrom":[subQ1,subQ0]});Q46=makeQuery(id+"F0.imprint","IMPRINT",FACE,{"disambiguationData":[TD([[makeQuery(id+"F0.imprint","IMPRINT",EDGE,{"disambiguationData":[TD([[subQ2,1.0]])],"derivedFrom":subQ1}),-1.0]])]});}
            var Q47;
            {var subQ0=sQuery(id+"F0.wireOp",EDGE,"E4.2.22.0");var subQ1=sQuery(id+"F0.wireOp",EDGE,"E0");var subQ2=makeQuery(id+"F0.imprint","INTERSECT",VERTEX,{"derivedFrom":[subQ1,subQ0]});Q47=makeQuery(id+"F0.imprint","IMPRINT",FACE,{"disambiguationData":[TD([[makeQuery(id+"F0.imprint","IMPRINT",EDGE,{"disambiguationData":[TD([[subQ2,1.0]])],"derivedFrom":subQ1}),-1.0]])]});}
            var Q48;
            {var subQ0=sQuery(id+"F0.wireOp",EDGE,"E4.2.6.0");var subQ1=sQuery(id+"F0.wireOp",EDGE,"E0");var subQ2=makeQuery(id+"F0.imprint","INTERSECT",VERTEX,{"derivedFrom":[subQ1,subQ0]});Q48=makeQuery(id+"F0.imprint","IMPRINT",FACE,{"disambiguationData":[TD([[makeQuery(id+"F0.imprint","IMPRINT",EDGE,{"disambiguationData":[TD([[subQ2,1.0]])],"derivedFrom":subQ1}),-1.0]])]});}
            var Q49;
            {var subQ0=sQuery(id+"F0.wireOp",EDGE,"E4.2.20.0");var subQ1=sQuery(id+"F0.wireOp",EDGE,"E0");var subQ2=makeQuery(id+"F0.imprint","INTERSECT",VERTEX,{"derivedFrom":[subQ1,subQ0]});Q49=makeQuery(id+"F0.imprint","IMPRINT",FACE,{"disambiguationData":[TD([[makeQuery(id+"F0.imprint","IMPRINT",EDGE,{"disambiguationData":[TD([[subQ2,1.0]])],"derivedFrom":subQ1}),-1.0]])]});}
            var Q50;
            {var subQ0=sQuery(id+"F0.wireOp",EDGE,"E4.2.12.0");var subQ1=sQuery(id+"F0.wireOp",EDGE,"E0");var subQ2=makeQuery(id+"F0.imprint","INTERSECT",VERTEX,{"derivedFrom":[subQ1,subQ0]});Q50=makeQuery(id+"F0.imprint","IMPRINT",FACE,{"disambiguationData":[TD([[makeQuery(id+"F0.imprint","IMPRINT",EDGE,{"disambiguationData":[TD([[subQ2,1.0]])],"derivedFrom":subQ1}),-1.0]])]});}
            var Q51;
            {var subQ0=sQuery(id+"F0.wireOp",EDGE,"E4.2.4.0");var subQ1=sQuery(id+"F0.wireOp",EDGE,"E0");var subQ2=makeQuery(id+"F0.imprint","INTERSECT",VERTEX,{"derivedFrom":[subQ1,subQ0]});Q51=makeQuery(id+"F0.imprint","IMPRINT",FACE,{"disambiguationData":[TD([[makeQuery(id+"F0.imprint","IMPRINT",EDGE,{"disambiguationData":[TD([[subQ2,1.0]])],"derivedFrom":subQ1}),-1.0]])]});}
            var Q52;
            {var subQ0=sQuery(id+"F0.wireOp",EDGE,"E3.1.0");var subQ1=sQuery(id+"F0.wireOp",EDGE,"E0");var subQ2=makeQuery(id+"F0.imprint","INTERSECT",VERTEX,{"derivedFrom":[subQ1,subQ0]});Q52=makeQuery(id+"F0.imprint","IMPRINT",FACE,{"disambiguationData":[TD([[makeQuery(id+"F0.imprint","IMPRINT",EDGE,{"disambiguationData":[TD([[subQ2,1.0]])],"derivedFrom":subQ1}),-1.0]])]});}
            var Q53;
            {var subQ0=sQuery(id+"F0.wireOp",EDGE,"E4.2.17.0");var subQ1=sQuery(id+"F0.wireOp",EDGE,"E0");var subQ2=makeQuery(id+"F0.imprint","INTERSECT",VERTEX,{"derivedFrom":[subQ1,subQ0]});Q53=makeQuery(id+"F0.imprint","IMPRINT",FACE,{"disambiguationData":[TD([[makeQuery(id+"F0.imprint","IMPRINT",EDGE,{"disambiguationData":[TD([[subQ2,1.0]])],"derivedFrom":subQ1}),-1.0]])]});}
            var Q54;
            {var subQ0=sQuery(id+"F0.wireOp",EDGE,"E1");var subQ1=sQuery(id+"F0.wireOp",EDGE,"E0");var subQ2=makeQuery(id+"F0.imprint","INTERSECT",VERTEX,{"derivedFrom":[subQ1,subQ0]});Q54=makeQuery(id+"F0.imprint","IMPRINT",FACE,{"disambiguationData":[TD([[makeQuery(id+"F0.imprint","IMPRINT",EDGE,{"disambiguationData":[TD([[subQ2,-1.0]])],"derivedFrom":subQ1}),-1.0]])]});}
            var Q55;
            {var subQ0=sQuery(id+"F0.wireOp",EDGE,"E4.2.16.0");var subQ1=sQuery(id+"F0.wireOp",EDGE,"E0");var subQ2=makeQuery(id+"F0.imprint","INTERSECT",VERTEX,{"derivedFrom":[subQ1,subQ0]});Q55=makeQuery(id+"F0.imprint","IMPRINT",FACE,{"disambiguationData":[TD([[makeQuery(id+"F0.imprint","IMPRINT",EDGE,{"disambiguationData":[TD([[subQ2,1.0]])],"derivedFrom":subQ1}),-1.0]])]});}
            var Q56;
            {var subQ0=sQuery(id+"F0.wireOp",EDGE,"E4.2.8.0");var subQ1=sQuery(id+"F0.wireOp",EDGE,"E0");var subQ2=makeQuery(id+"F0.imprint","INTERSECT",VERTEX,{"derivedFrom":[subQ1,subQ0]});Q56=makeQuery(id+"F0.imprint","IMPRINT",FACE,{"disambiguationData":[TD([[makeQuery(id+"F0.imprint","IMPRINT",EDGE,{"disambiguationData":[TD([[subQ2,1.0]])],"derivedFrom":subQ1}),-1.0]])]});}
            var Q57;
            {var subQ0=sQuery(id+"F0.wireOp",EDGE,"E4.2.25.0");var subQ1=sQuery(id+"F0.wireOp",EDGE,"E0");var subQ2=makeQuery(id+"F0.imprint","INTERSECT",VERTEX,{"derivedFrom":[subQ1,subQ0]});Q57=makeQuery(id+"F0.imprint","IMPRINT",FACE,{"disambiguationData":[TD([[makeQuery(id+"F0.imprint","IMPRINT",EDGE,{"disambiguationData":[TD([[subQ2,1.0]])],"derivedFrom":subQ1}),-1.0]])]});}
            var Q58;
            {var subQ0=sQuery(id+"F0.wireOp",EDGE,"E4.2.26.0");var subQ1=sQuery(id+"F0.wireOp",EDGE,"E0");var subQ2=makeQuery(id+"F0.imprint","INTERSECT",VERTEX,{"derivedFrom":[subQ1,subQ0]});Q58=makeQuery(id+"F0.imprint","IMPRINT",FACE,{"disambiguationData":[TD([[makeQuery(id+"F0.imprint","IMPRINT",EDGE,{"disambiguationData":[TD([[subQ2,1.0]])],"derivedFrom":subQ1}),-1.0]])]});}
            var Q59;
            {var subQ0=sQuery(id+"F0.wireOp",EDGE,"E4.2.27.0");var subQ1=sQuery(id+"F0.wireOp",EDGE,"E0");var subQ2=makeQuery(id+"F0.imprint","INTERSECT",VERTEX,{"derivedFrom":[subQ1,subQ0]});Q59=makeQuery(id+"F0.imprint","IMPRINT",FACE,{"disambiguationData":[TD([[makeQuery(id+"F0.imprint","IMPRINT",EDGE,{"disambiguationData":[TD([[subQ2,1.0]])],"derivedFrom":subQ1}),-1.0]])]});}
            var Q60;
            {var subQ0=sQuery(id+"F0.wireOp",EDGE,"E4.2.29.0");var subQ1=sQuery(id+"F0.wireOp",EDGE,"E0");var subQ2=makeQuery(id+"F0.imprint","INTERSECT",VERTEX,{"derivedFrom":[subQ1,subQ0]});Q60=makeQuery(id+"F0.imprint","IMPRINT",FACE,{"disambiguationData":[TD([[makeQuery(id+"F0.imprint","IMPRINT",EDGE,{"disambiguationData":[TD([[subQ2,1.0]])],"derivedFrom":subQ1}),-1.0]])]});}
            var Q61;
            {var subQ0=sQuery(id+"F0.wireOp",EDGE,"E4.2.30.0");var subQ1=sQuery(id+"F0.wireOp",EDGE,"E0");var subQ2=makeQuery(id+"F0.imprint","INTERSECT",VERTEX,{"derivedFrom":[subQ1,subQ0]});Q61=makeQuery(id+"F0.imprint","IMPRINT",FACE,{"disambiguationData":[TD([[makeQuery(id+"F0.imprint","IMPRINT",EDGE,{"disambiguationData":[TD([[subQ2,1.0]])],"derivedFrom":subQ1}),-1.0]])]});}
            var Q62;
            {var subQ0=sQuery(id+"F0.wireOp",EDGE,"E4.2.15.0");var subQ1=sQuery(id+"F0.wireOp",EDGE,"E0");var subQ2=makeQuery(id+"F0.imprint","INTERSECT",VERTEX,{"derivedFrom":[subQ1,subQ0]});Q62=makeQuery(id+"F0.imprint","IMPRINT",FACE,{"disambiguationData":[TD([[makeQuery(id+"F0.imprint","IMPRINT",EDGE,{"disambiguationData":[TD([[subQ2,1.0]])],"derivedFrom":subQ1}),-1.0]])]});}
            var Q63;
            {var subQ0=sQuery(id+"F0.wireOp",EDGE,"E4.2.14.0");var subQ1=sQuery(id+"F0.wireOp",EDGE,"E0");var subQ2=makeQuery(id+"F0.imprint","INTERSECT",VERTEX,{"derivedFrom":[subQ1,subQ0]});Q63=makeQuery(id+"F0.imprint","IMPRINT",FACE,{"disambiguationData":[TD([[makeQuery(id+"F0.imprint","IMPRINT",EDGE,{"disambiguationData":[TD([[subQ2,1.0]])],"derivedFrom":subQ1}),-1.0]])]});}
            var Q64;
            {var subQ0=sQuery(id+"F0.wireOp",EDGE,"E4.2.9.0");var subQ1=sQuery(id+"F0.wireOp",EDGE,"E0");var subQ2=makeQuery(id+"F0.imprint","INTERSECT",VERTEX,{"derivedFrom":[subQ1,subQ0]});Q64=makeQuery(id+"F0.imprint","IMPRINT",FACE,{"disambiguationData":[TD([[makeQuery(id+"F0.imprint","IMPRINT",EDGE,{"disambiguationData":[TD([[subQ2,1.0]])],"derivedFrom":subQ1}),-1.0]])]});}
            extrude(context, id + "F1", {"entities" : qUnion([Q0, Q1, Q2, Q3, Q4, Q5, Q6, Q7, Q8, Q9, Q10, Q11, Q12, Q13, Q14, Q15, Q16, Q17, Q18, Q19, Q20, Q21, Q22, Q23, Q24, Q25, Q26, Q27, Q28, Q29, Q30, Q31, Q32, Q33, Q34, Q35, Q36, Q37, Q38, Q39, Q40, Q41, Q42, Q43, Q44, Q45, Q46, Q47, Q48, Q49, Q50, Q51, Q52, Q53, Q54, Q55, Q56, Q57, Q58, Q59, Q60, Q61, Q62, Q63, Q64]), "depth" : 5.08 * mm});
        }
        {
            var Q0;
            Q0=makeQuery(id+"F1.opExtrude","CAP_FACE",FACE,{"disambiguationData":[OSD([sQuery(id+"F0.wireOp",EDGE,"E1"),sQuery(id+"F0.wireOp",EDGE,"E2"),sQuery(id+"F0.wireOp",EDGE,"E3.1.0"),sQuery(id+"F0.wireOp",EDGE,"E3.1.1"),sQuery(id+"F0.wireOp",EDGE,"E3.2.0"),sQuery(id+"F0.wireOp",EDGE,"E3.2.1"),sQuery(id+"F0.wireOp",EDGE,"E4.2.3.0"),sQuery(id+"F0.wireOp",EDGE,"E4.3.3.0"),sQuery(id+"F0.wireOp",EDGE,"E4.2.4.0"),sQuery(id+"F0.wireOp",EDGE,"E4.3.4.0"),sQuery(id+"F0.wireOp",EDGE,"E4.2.5.0"),sQuery(id+"F0.wireOp",EDGE,"E4.3.5.0"),sQuery(id+"F0.wireOp",EDGE,"E4.2.6.0"),sQuery(id+"F0.wireOp",EDGE,"E4.3.6.0"),sQuery(id+"F0.wireOp",EDGE,"E4.2.7.0"),sQuery(id+"F0.wireOp",EDGE,"E4.3.7.0"),sQuery(id+"F0.wireOp",EDGE,"E4.2.8.0"),sQuery(id+"F0.wireOp",EDGE,"E4.3.8.0"),sQuery(id+"F0.wireOp",EDGE,"E4.2.9.0"),sQuery(id+"F0.wireOp",EDGE,"E4.3.9.0"),sQuery(id+"F0.wireOp",EDGE,"E4.2.10.0"),sQuery(id+"F0.wireOp",EDGE,"E4.3.10.0"),sQuery(id+"F0.wireOp",EDGE,"E4.2.11.0"),sQuery(id+"F0.wireOp",EDGE,"E4.3.11.0"),sQuery(id+"F0.wireOp",EDGE,"E4.2.12.0"),sQuery(id+"F0.wireOp",EDGE,"E4.3.12.0"),sQuery(id+"F0.wireOp",EDGE,"E4.2.13.0"),sQuery(id+"F0.wireOp",EDGE,"E4.3.13.0"),sQuery(id+"F0.wireOp",EDGE,"E4.2.14.0"),sQuery(id+"F0.wireOp",EDGE,"E4.3.14.0"),sQuery(id+"F0.wireOp",EDGE,"E4.2.15.0"),sQuery(id+"F0.wireOp",EDGE,"E4.3.15.0"),sQuery(id+"F0.wireOp",EDGE,"E4.2.16.0"),sQuery(id+"F0.wireOp",EDGE,"E4.3.16.0"),sQuery(id+"F0.wireOp",EDGE,"E4.2.17.0"),sQuery(id+"F0.wireOp",EDGE,"E4.3.17.0"),sQuery(id+"F0.wireOp",EDGE,"E4.2.18.0"),sQuery(id+"F0.wireOp",EDGE,"E4.3.18.0"),sQuery(id+"F0.wireOp",EDGE,"E4.2.19.0"),sQuery(id+"F0.wireOp",EDGE,"E4.3.19.0"),sQuery(id+"F0.wireOp",EDGE,"E4.2.20.0"),sQuery(id+"F0.wireOp",EDGE,"E4.3.20.0"),sQuery(id+"F0.wireOp",EDGE,"E4.2.21.0"),sQuery(id+"F0.wireOp",EDGE,"E4.3.21.0"),sQuery(id+"F0.wireOp",EDGE,"E4.2.22.0"),sQuery(id+"F0.wireOp",EDGE,"E4.3.22.0"),sQuery(id+"F0.wireOp",EDGE,"E4.2.23.0"),sQuery(id+"F0.wireOp",EDGE,"E4.3.23.0"),sQuery(id+"F0.wireOp",EDGE,"E4.2.24.0"),sQuery(id+"F0.wireOp",EDGE,"E4.3.24.0"),sQuery(id+"F0.wireOp",EDGE,"E4.2.25.0"),sQuery(id+"F0.wireOp",EDGE,"E4.3.25.0"),sQuery(id+"F0.wireOp",EDGE,"E4.2.26.0"),sQuery(id+"F0.wireOp",EDGE,"E4.3.26.0"),sQuery(id+"F0.wireOp",EDGE,"E4.2.27.0"),sQuery(id+"F0.wireOp",EDGE,"E4.3.27.0"),sQuery(id+"F0.wireOp",EDGE,"E4.2.28.0"),sQuery(id+"F0.wireOp",EDGE,"E4.3.28.0"),sQuery(id+"F0.wireOp",EDGE,"E4.2.29.0"),sQuery(id+"F0.wireOp",EDGE,"E4.3.29.0"),sQuery(id+"F0.wireOp",EDGE,"E4.2.30.0"),sQuery(id+"F0.wireOp",EDGE,"E4.3.30.0"),sQuery(id+"F0.wireOp",EDGE,"E4.2.31.0"),sQuery(id+"F0.wireOp",EDGE,"E4.3.31.0")])],"isStart":false});
            var sketch = newSketch(context, id + "F2", { "sketchPlane" : qUnion([Q0])});
            skCircle(sketch, "E5", {"center": v(0, 0) * mm, "radius": 2.76 * mm});
            skLineSegment(sketch, "E6", {"start": v(-0.73, 2.66) * mm, "end": v(0, 5.04) * mm});
            skLineSegment(sketch, "E7", {"start": v(0, 5.04) * mm, "end": v(0.8, 2.64) * mm});
            skLineSegment(sketch, "E8.1.0", {"start": v(-2.96, 4.08) * mm, "end": v(-0.9, 2.6) * mm});
            skLineSegment(sketch, "E8.1.1", {"start": v(-2.15, 1.72) * mm, "end": v(-2.96, 4.08) * mm});
            skLineSegment(sketch, "E8.2.0", {"start": v(-4.8, 1.56) * mm, "end": v(-2.26, 1.57) * mm});
            skLineSegment(sketch, "E8.2.1", {"start": v(-2.75, 0.13) * mm, "end": v(-4.8, 1.56) * mm});
            skLineSegment(sketch, "E8.3.0", {"start": v(-4.8, -1.56) * mm, "end": v(-2.75, -0.06) * mm});
            skLineSegment(sketch, "E8.3.1", {"start": v(-2.3, -1.51) * mm, "end": v(-4.8, -1.56) * mm});
            skLineSegment(sketch, "E8.4.0", {"start": v(-2.96, -4.08) * mm, "end": v(-2.2, -1.66) * mm});
            skLineSegment(sketch, "E8.4.1", {"start": v(-0.98, -2.58) * mm, "end": v(-2.96, -4.08) * mm});
            skLineSegment(sketch, "E8.5.0", {"start": v(0, -5.04) * mm, "end": v(-0.8, -2.64) * mm});
            skLineSegment(sketch, "E8.5.1", {"start": v(0.73, -2.66) * mm, "end": v(0, -5.04) * mm});
            skLineSegment(sketch, "E8.6.0", {"start": v(2.96, -4.08) * mm, "end": v(0.9, -2.6) * mm});
            skLineSegment(sketch, "E8.6.1", {"start": v(2.15, -1.72) * mm, "end": v(2.96, -4.08) * mm});
            skLineSegment(sketch, "E8.7.0", {"start": v(4.8, -1.56) * mm, "end": v(2.26, -1.57) * mm});
            skLineSegment(sketch, "E8.7.1", {"start": v(2.75, -0.13) * mm, "end": v(4.8, -1.56) * mm});
            skLineSegment(sketch, "E8.8.0", {"start": v(4.8, 1.56) * mm, "end": v(2.75, 0.06) * mm});
            skLineSegment(sketch, "E8.8.1", {"start": v(2.3, 1.51) * mm, "end": v(4.8, 1.56) * mm});
            skLineSegment(sketch, "E8.9.0", {"start": v(2.96, 4.08) * mm, "end": v(2.2, 1.66) * mm});
            skLineSegment(sketch, "E8.9.1", {"start": v(0.98, 2.58) * mm, "end": v(2.96, 4.08) * mm});
            skSolve(sketch);
        }
        {
            var Q0;
            Q0 = qSketchRegion(id + "F2", true);
            extrude(context, id + "F3", {"entities" : qUnion([Q0]), "operationType" : NewBodyOperationType.ADD, "depth" : 7.62 * mm});
        }
        {
            var Q0;
            Q0=makeQuery(id+"F3.opExtrude","CAP_FACE",FACE,{"disambiguationData":[OSD([sQuery(id+"F2.wireOp",EDGE,"E5"),sQuery(id+"F2.wireOp",EDGE,"E6"),sQuery(id+"F2.wireOp",EDGE,"E7"),sQuery(id+"F2.wireOp",EDGE,"E8.1.0"),sQuery(id+"F2.wireOp",EDGE,"E8.1.1"),sQuery(id+"F2.wireOp",EDGE,"E8.2.0"),sQuery(id+"F2.wireOp",EDGE,"E8.2.1"),sQuery(id+"F2.wireOp",EDGE,"E8.3.0"),sQuery(id+"F2.wireOp",EDGE,"E8.3.1"),sQuery(id+"F2.wireOp",EDGE,"E8.4.0"),sQuery(id+"F2.wireOp",EDGE,"E8.4.1"),sQuery(id+"F2.wireOp",EDGE,"E8.5.0"),sQuery(id+"F2.wireOp",EDGE,"E8.5.1"),sQuery(id+"F2.wireOp",EDGE,"E8.6.0"),sQuery(id+"F2.wireOp",EDGE,"E8.6.1"),sQuery(id+"F2.wireOp",EDGE,"E8.7.0"),sQuery(id+"F2.wireOp",EDGE,"E8.7.1"),sQuery(id+"F2.wireOp",EDGE,"E8.8.0"),sQuery(id+"F2.wireOp",EDGE,"E8.8.1"),sQuery(id+"F2.wireOp",EDGE,"E8.9.0"),sQuery(id+"F2.wireOp",EDGE,"E8.9.1")])],"isStart":false});
            var sketch = newSketch(context, id + "F4", { "sketchPlane" : qUnion([Q0])});
            skCircle(sketch, "E9", {"center": v(0, 0) * mm, "radius": 1.52 * mm});
            skSolve(sketch);
        }
        {
            var Q0;
            Q0=makeQuery(id+"F4.imprint","IMPRINT",FACE,{"disambiguationData":[TD([[makeQuery(id+"F4.imprint","IMPRINT",EDGE,{"derivedFrom":sQuery(id+"F4.wireOp",EDGE,"E9")}),1.0]])]});
            extrude(context, id + "F5", {"entities" : qUnion([Q0]), "operationType" : NewBodyOperationType.REMOVE, "oppositeDirection" : true, "depth" : 12.7 * mm});
        }
    });
